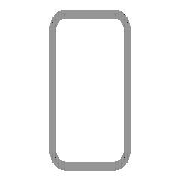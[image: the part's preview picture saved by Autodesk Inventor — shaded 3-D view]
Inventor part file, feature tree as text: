
AUTODESK INVENTOR PART (.ipt)
format: ipt  version: 2025 (Build 290162010, 162A)  size: 157,696 bytes
history: native  units: mm (DEFAULTED — no unit token found)
features: other x3, sketch x2, projected_geometry x2, extrude x1, plane x1
ambient origin geometry x8: Origin, YZ Plane, XZ Plane, XY Plane, X Axis, Y Axis, Z Axis, Center Point
bodies: Solid1 (feature_tree), Body (feature_tree)
feature tree (9):
  other  "Driven Length"
  other  "Start plane"
  other  "End plane"
  extrude  "Extrusion4"  TaperAngle=0.0deg  [1 undecoded]
  sketch  "Sketch3"  dims[d3=2800.0mm d4=0.0mm]
  plane  "Work Plane3"
  sketch  "Sketch7"  dims[d7=6.0mm d9=40.0mm d11=60.0mm d12=3.0mm d13=-0.0mm d14=2800.0mm d15=20.0mm d16=30.0mm d17=90.0deg d18=2800.0mm d26=45.0deg d27=45.0deg d28=0.0mm d29=0.0mm]
  projected_geometry  "Projected Loop1"
  projected_geometry  "Projected Loop2"
note: 1 required parameter value undecoded (feature->parameter linkage not recoverable at this tier; creation-order binding heuristic only, values carry confidence <= 0.55)
